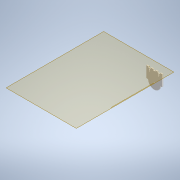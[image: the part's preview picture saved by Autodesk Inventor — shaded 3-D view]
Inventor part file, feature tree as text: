
AUTODESK INVENTOR PART (.ipt)
format: ipt  version: 2021.1 (Build 251245010, 245A)  size: 175,104 bytes
history: native  units: mm
features: other x8, reference x6, extrude x2, sketch x1
ambient origin geometry x8: Origin, YZ Plane, XZ Plane, XY Plane, X Axis, Y Axis, Z Axis, Center Point
bodies: Body1 (feature_tree)
feature tree (17):
  other  "Твердое тело1"
  other  "РабПлоскость1"
  other  "РабОсь1"
  extrude  "Выдавливание1"  Depth=57.0mm
  extrude  "Выдавливание2"  Depth=34.0mm
  reference  "Ссылка1"
  reference  "Ссылка2"
  reference  "Ссылка3"
  reference  "Ссылка4"
  other  "РабПлоскость2"
  sketch  "Эскиз2"
  reference  "Ссылка8"
  reference  "Ссылка9"
  other  "<userpath>\Documents\Savka\3d\Korp.iam"
  other  "Korp.iam"
  other  "Korpus 3:1"
  other  "Korpus:1"
